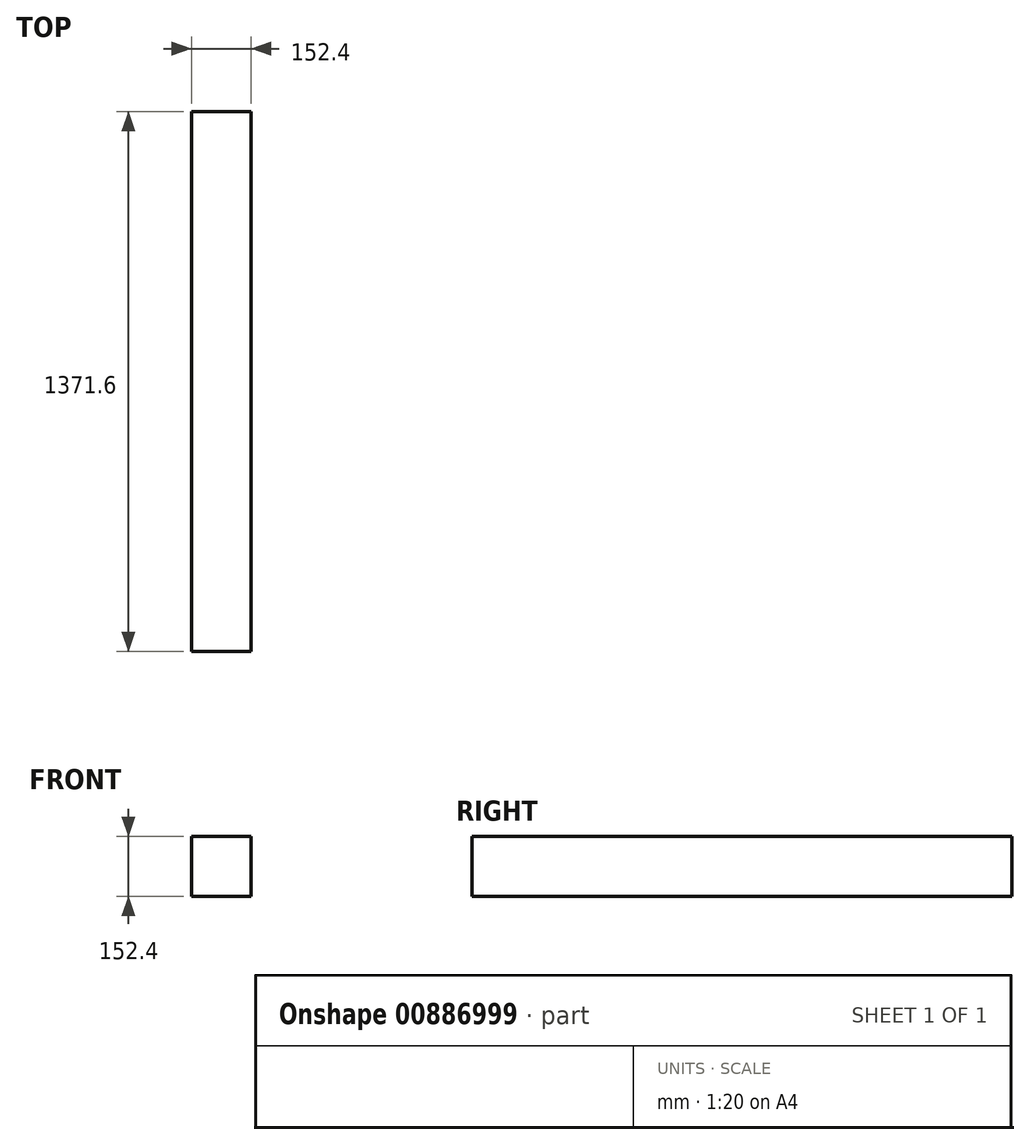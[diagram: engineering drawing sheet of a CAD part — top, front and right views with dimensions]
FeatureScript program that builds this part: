
annotation { "Feature Type Name" : "Feature", "Feature Type Description" : "" }
export const myFeature = defineFeature(function(context is Context, id is Id, definition is map)
    precondition{}
    {
        {
            var Q0;
            Q0=qCreatedBy(makeId("Front.planeOp"),FACE);
            var sketch = newSketch(context, id + "F0", { "sketchPlane" : qUnion([Q0])});
            skLineSegment(sketch, "E0.bottom", {"start": v(0, 0) * mm, "end": v(152.4, 0) * mm});
            skLineSegment(sketch, "E0.top", {"start": v(0, 152.4) * mm, "end": v(152.4, 152.4) * mm});
            skLineSegment(sketch, "E0.left", {"start": v(0, 0) * mm, "end": v(0, 152.4) * mm});
            skLineSegment(sketch, "E0.right", {"start": v(152.4, 0) * mm, "end": v(152.4, 152.4) * mm});
            skSolve(sketch);
        }
        {
            var Q0;
            Q0 = qSketchRegion(id + "F0", true);
            extrude(context, id + "F1", {"entities" : qUnion([Q0]), "depth" : 1371.6 * mm, "offsetDistance" : 25.4 * mm});
        }
    });
